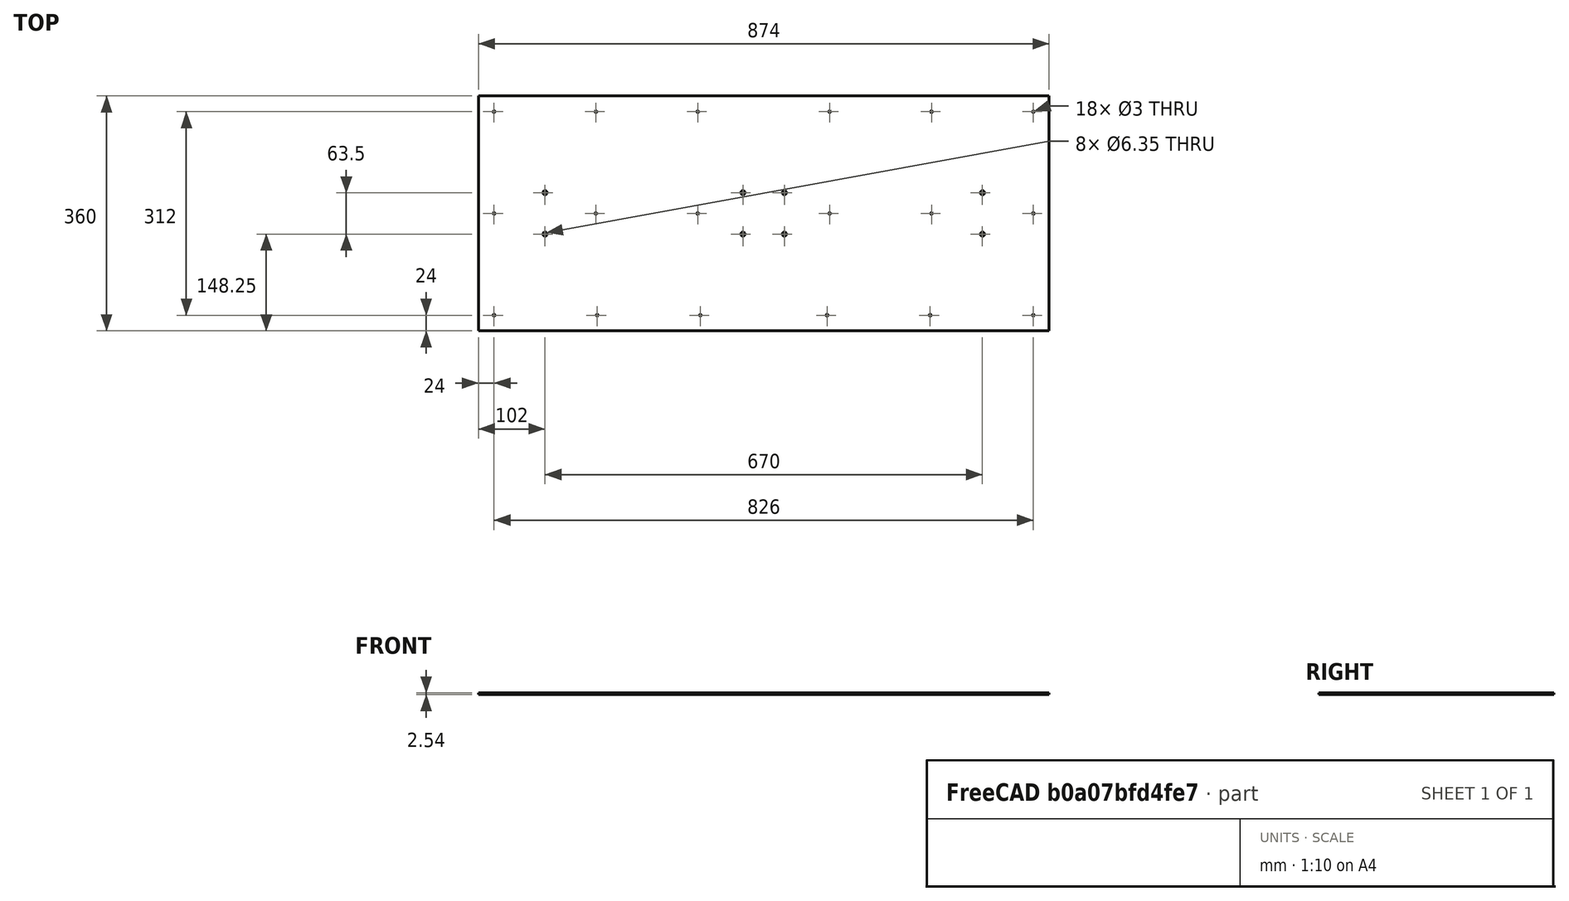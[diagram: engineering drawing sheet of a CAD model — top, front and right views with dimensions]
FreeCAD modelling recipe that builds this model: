
FCSTD DOCUMENT  (FreeCAD 0.21R33771 (Git))
Label: top_panel
License: All rights reserved
LicenseURL: https://en.wikipedia.org/wiki/All_rights_reserved
objects: Sketcher::SketchObject×1, PartDesign::Pad×1, PartDesign::Body×1
note: 4 computed .brp shape members not serialized (recipe doc carries the construction recipe); baked Part::Feature solids carry a one-line shape summary decoded from their .brp

FEATURE [Sketcher::SketchObject] Sketch
  FullyConstrained = false
  MapMode = 2
  sketch-geometry (31):
    g0: LineSegment StartX=-437 StartY=180 StartZ=0 EndX=437 EndY=180 EndZ=0
    g1: LineSegment StartX=437 StartY=180 StartZ=0 EndX=437 EndY=-180 EndZ=0
    g2: LineSegment StartX=437 StartY=-180 StartZ=0 EndX=-437 EndY=-180 EndZ=0
    g3: LineSegment StartX=-437 StartY=-180 StartZ=0 EndX=-437 EndY=180 EndZ=0
    g4: Circle CenterX=-413 CenterY=-1.02831e-05 CenterZ=0 NormalX=0 NormalY=0 NormalZ=1 AngleXU=0 Radius=1.5
    g5: Circle CenterX=-413 CenterY=-156 CenterZ=0 NormalX=0 NormalY=0 NormalZ=1 AngleXU=0 Radius=1.5
    g6: Circle CenterX=-335 CenterY=31.75 CenterZ=0 NormalX=0 NormalY=0 NormalZ=1 AngleXU=0 Radius=3.175
    g7: Circle CenterX=-257 CenterY=156 CenterZ=0 NormalX=0 NormalY=0 NormalZ=1 AngleXU=0 Radius=1.4986
    g8: Circle CenterX=-335 CenterY=-31.75 CenterZ=0 NormalX=0 NormalY=0 NormalZ=1 AngleXU=0 Radius=3.175
    g9: Circle CenterX=-257 CenterY=0 CenterZ=0 NormalX=0 NormalY=0 NormalZ=1 AngleXU=0 Radius=1.5
    g10: Circle CenterX=-255 CenterY=-156 CenterZ=0 NormalX=0 NormalY=0 NormalZ=1 AngleXU=0 Radius=1.5
    g11: Circle CenterX=-101 CenterY=156 CenterZ=0 NormalX=0 NormalY=0 NormalZ=1 AngleXU=0 Radius=1.5
    g12: Circle CenterX=-101 CenterY=0 CenterZ=0 NormalX=0 NormalY=0 NormalZ=1 AngleXU=0 Radius=1.5
    g13: Circle CenterX=-97 CenterY=-156 CenterZ=0 NormalX=0 NormalY=0 NormalZ=1 AngleXU=0 Radius=1.5
    g14: LineSegment StartX=0 StartY=180 StartZ=0 EndX=0 EndY=-180 EndZ=0
    g15: Circle CenterX=413 CenterY=156 CenterZ=0 NormalX=0 NormalY=0 NormalZ=1 AngleXU=0 Radius=1.5
    g16: Circle CenterX=413 CenterY=-1.21668e-11 CenterZ=0 NormalX=0 NormalY=0 NormalZ=1 AngleXU=0 Radius=1.5
    g17: Circle CenterX=413 CenterY=-156 CenterZ=0 NormalX=0 NormalY=0 NormalZ=1 AngleXU=0 Radius=1.5
    g18: Circle CenterX=335 CenterY=31.75 CenterZ=0 NormalX=0 NormalY=0 NormalZ=1 AngleXU=0 Radius=3.175
    g19: Circle CenterX=257 CenterY=156 CenterZ=0 NormalX=0 NormalY=0 NormalZ=1 AngleXU=0 Radius=1.5
    g20: Circle CenterX=335 CenterY=-31.75 CenterZ=0 NormalX=0 NormalY=0 NormalZ=1 AngleXU=0 Radius=3.175
    g21: Circle CenterX=257 CenterY=0 CenterZ=0 NormalX=0 NormalY=0 NormalZ=1 AngleXU=0 Radius=1.5
    g22: Circle CenterX=255 CenterY=-156 CenterZ=0 NormalX=0 NormalY=0 NormalZ=1 AngleXU=0 Radius=1.5
    g23: Circle CenterX=101 CenterY=156 CenterZ=0 NormalX=0 NormalY=0 NormalZ=1 AngleXU=0 Radius=1.5
    g24: Circle CenterX=101 CenterY=0 CenterZ=0 NormalX=0 NormalY=0 NormalZ=1 AngleXU=0 Radius=1.5
    g25: Circle CenterX=97 CenterY=-156 CenterZ=0 NormalX=0 NormalY=0 NormalZ=1 AngleXU=0 Radius=1.5
    g26: Circle CenterX=-31.75 CenterY=31.75 CenterZ=0 NormalX=0 NormalY=0 NormalZ=1 AngleXU=0 Radius=3.175
    g27: Circle CenterX=-31.75 CenterY=-31.75 CenterZ=0 NormalX=0 NormalY=0 NormalZ=1 AngleXU=0 Radius=3.175
    g28: Circle CenterX=31.75 CenterY=31.75 CenterZ=0 NormalX=0 NormalY=0 NormalZ=1 AngleXU=0 Radius=3.175
    g29: Circle CenterX=31.75 CenterY=-31.75 CenterZ=0 NormalX=0 NormalY=0 NormalZ=1 AngleXU=0 Radius=3.175
    g30: Circle CenterX=-413 CenterY=156 CenterZ=0 NormalX=0 NormalY=0 NormalZ=1 AngleXU=0 Radius=1.4986
  constraints (65):
    c: Coincident(g0,g1)
    c: Coincident(g1,g2)
    c: Coincident(g2,g3)
    c: Coincident(g3,g0)
    c: Horizontal(g0)
    c: Horizontal(g2)
    c: Vertical(g1)
    c: DistanceX(g0,g0) = 874
    c: DistanceY(g1,g1) = 360
    c: Diameter(g4) = 3
    c: Diameter(g5) = 3
    c: Diameter(g6) = 6.35
    c: Diameter(g7) = 2.9972
    c: Diameter(g8) = 6.35
    c: Distance(g4,g3) = 24
    c: Distance(g5,g3) = 24
    c: Diameter(g9) = 3
    c: Diameter(g10) = 3
    c: Distance(g4,g5) = 156
    c: DistanceX(g4,g8) = 78
    c: DistanceX(g6,g9) = 78
    c: Distance(g7,g0) = 24
    c: DistanceX(g5,g10) = 158
    c: Distance(g10,g2) = 24
    c: Diameter(g11) = 3
    c: Diameter(g12) = 3
    c: Diameter(g13) = 3
    c: DistanceX(g7,g11) = 156
    c: Distance(g11,g0) = 24
    c: DistanceX(g4,g6) = 78
    c: DistanceX(g9,g12) = 156
    c: DistanceX(g10,g13) = 158
    c: Distance(g13,g2) = 24
    c: PointOnObject(g14,g0)
    c: PointOnObject(g14,g2)
    c: Vertical(g14)
    c: DistanceX(g14,g0) = 437
    c: Symmetric(g0,g2,g-1)
    c: Distance(g6,g-1) = 31.75
    c: Distance(g8,g-1) = 31.75
    c: PointOnObject(g9,g-1)
    c: PointOnObject(g12,g-1)
    c: PointOnObject(g-1,g14)
    c: Diameter(g15) = 3
    c: Diameter(g16) = 3
    c: Diameter(g17) = 3
    c: Diameter(g18) = 6.35
    c: Diameter(g19) = 3
    c: Diameter(g20) = 6.35
    c: Distance(g15,g16) = 156
    c: Diameter(g21) = 3
    c: Diameter(g22) = 3
    c: Distance(g16,g17) = 156
    c: Diameter(g23) = 3
    c: Diameter(g24) = 3
    c: Diameter(g25) = 3
    c: Diameter(g26) = 6.35
    c: Distance(g26,g-1) = 31.75
    c: Distance(g26,g14) = 31.75
    c: Diameter(g27) = 6.35
    c: Diameter(g28) = 6.35
    c: Diameter(g29) = 6.35
    c: Diameter(g30) = 2.9972
    c: Distance(g30,g3) = 24
    c: Distance(g30,g0) = 24
FEATURE [PartDesign::Pad] Pad
  Direction = (0,0,1)
  Length = 2.54
  Length2 = 10
  Profile = -> Sketch
  ReferenceAxis = -> Sketch [N_Axis]
  Type = 0
FEATURE [PartDesign::Body] Body
  Group = -> [Sketch,Pad]
  Origin = -> Origin001
  Tip = -> Pad
